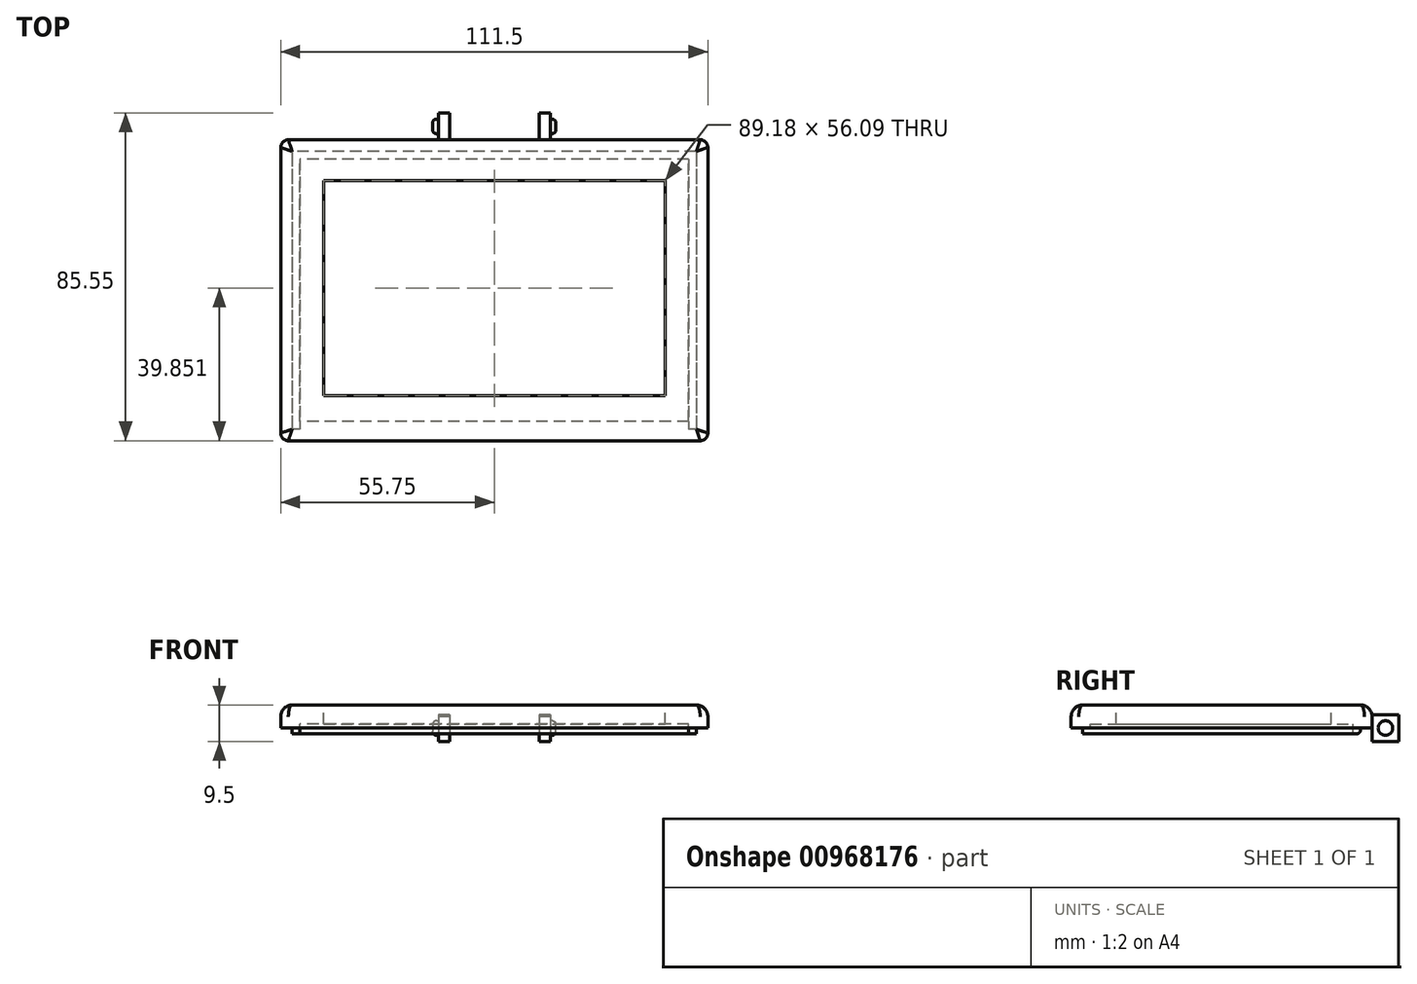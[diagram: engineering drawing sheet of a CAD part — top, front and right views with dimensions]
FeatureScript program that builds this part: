
annotation { "Feature Type Name" : "Feature", "Feature Type Description" : "" }
export const myFeature = defineFeature(function(context is Context, id is Id, definition is map)
    precondition{}
    {
        {
            var Q0;
            Q0=qCreatedBy(makeId("Top.planeOp"),FACE);
            cPlane(context, id + "F0", {"entities" : qUnion([Q0]), "cplaneType" : CPlaneType.OFFSET, "offset" : 3.5 * mm, "width" : 150 * mm, "height" : 150 * mm});
        }
        {
            var Q0;
            Q0=qCreatedBy(id+"F0.planeOp",FACE);
            var sketch = newSketch(context, id + "F1", { "sketchPlane" : qUnion([Q0])});
            skLineSegment(sketch, "E0.bottom", {"start": v(47.75, 31.27) * mm, "end": v(-47.75, 31.27) * mm});
            skLineSegment(sketch, "E0.top", {"start": v(47.75, -31.27) * mm, "end": v(-47.75, -31.27) * mm});
            skLineSegment(sketch, "E0.left", {"start": v(47.75, 31.27) * mm, "end": v(47.75, -31.27) * mm});
            skLineSegment(sketch, "E0.right", {"start": v(-47.75, 31.27) * mm, "end": v(-47.75, -31.27) * mm});
            skPoint(sketch, "E0.middle", {"position": v(0, 0) * mm});
            skLineSegment(sketch, "E1.0", {"start": v(-55.75, 39.27) * mm, "end": v(-55.75, -39.27) * mm});
            skLineSegment(sketch, "E1.1", {"start": v(55.75, 39.27) * mm, "end": v(-55.75, 39.27) * mm});
            skLineSegment(sketch, "E1.2", {"start": v(55.75, 39.27) * mm, "end": v(55.75, -39.27) * mm});
            skLineSegment(sketch, "E1.3", {"start": v(55.75, -39.27) * mm, "end": v(-55.75, -39.27) * mm});
            skSolve(sketch);
        }
        {
            var Q0;
            Q0=qCreatedBy(id+"F0.planeOp",FACE);
            var sketch = newSketch(context, id + "F2", { "sketchPlane" : qUnion([Q0])});
            skLineSegment(sketch, "E2.0", {"start": v(55.75, 39.27) * mm, "end": v(-55.75, 39.27) * mm});
            skLineSegment(sketch, "E3.0", {"start": v(-55.75, 39.27) * mm, "end": v(-55.75, -39.27) * mm});
            skLineSegment(sketch, "E4.0", {"start": v(55.75, -39.27) * mm, "end": v(-55.75, -39.27) * mm});
            skLineSegment(sketch, "E5.0", {"start": v(55.75, 39.27) * mm, "end": v(55.75, -39.27) * mm});
            skSolve(sketch);
        }
        {
            var Q0;
            Q0 = qSketchRegion(id + "F2", true);
            extrude(context, id + "F3", {"entities" : qUnion([Q0]), "depth" : 6 * mm, "offsetDistance" : 25 * mm});
        }
        {
            var Q0;
            Q0=makeQuery(id+"F3.opExtrude","CAP_FACE",FACE,{"disambiguationData":[OSD([sQuery(id+"F2.wireOp",EDGE,"E2.0"),sQuery(id+"F2.wireOp",EDGE,"E3.0"),sQuery(id+"F2.wireOp",EDGE,"E4.0"),sQuery(id+"F2.wireOp",EDGE,"E5.0")])],"isStart":false});
            fillet(context, id + "F4", {"entities" : qUnion([Q0]), "radius" : 3 * mm, "tangentPropagation" : true, "allowEdgeOverflow" : false});
        }
        {
            var Q0;
            Q0=makeQuery(id+"F4.opFillet","BLEND_EDGE",EDGE,{"blendedFrom":[makeQuery(id+"F3.opExtrude","CAP_EDGE",EDGE,{"disambiguationData":[OSD([sQuery(id+"F2.wireOp",EDGE,"E4.0")])],"isStart":false}),makeQuery(id+"F3.opExtrude","CAP_EDGE",EDGE,{"disambiguationData":[OSD([sQuery(id+"F2.wireOp",EDGE,"E5.0")])],"isStart":false})],"blendedInto":[]});
            var Q1;
            Q1=makeQuery(id+"F4.opFillet","BLEND_EDGE",EDGE,{"blendedFrom":[makeQuery(id+"F3.opExtrude","CAP_EDGE",EDGE,{"disambiguationData":[OSD([sQuery(id+"F2.wireOp",EDGE,"E2.0")])],"isStart":false}),makeQuery(id+"F3.opExtrude","CAP_EDGE",EDGE,{"disambiguationData":[OSD([sQuery(id+"F2.wireOp",EDGE,"E5.0")])],"isStart":false})],"blendedInto":[]});
            var Q2;
            Q2=makeQuery(id+"F4.opFillet","BLEND_EDGE",EDGE,{"blendedFrom":[makeQuery(id+"F3.opExtrude","CAP_EDGE",EDGE,{"disambiguationData":[OSD([sQuery(id+"F2.wireOp",EDGE,"E3.0")])],"isStart":false}),makeQuery(id+"F3.opExtrude","CAP_EDGE",EDGE,{"disambiguationData":[OSD([sQuery(id+"F2.wireOp",EDGE,"E4.0")])],"isStart":false})],"blendedInto":[]});
            var Q3;
            Q3=makeQuery(id+"F4.opFillet","BLEND_EDGE",EDGE,{"blendedFrom":[makeQuery(id+"F3.opExtrude","CAP_EDGE",EDGE,{"disambiguationData":[OSD([sQuery(id+"F2.wireOp",EDGE,"E2.0")])],"isStart":false}),makeQuery(id+"F3.opExtrude","CAP_EDGE",EDGE,{"disambiguationData":[OSD([sQuery(id+"F2.wireOp",EDGE,"E3.0")])],"isStart":false})],"blendedInto":[]});
            fillet(context, id + "F5", {"entities" : qUnion([Q0, Q1, Q2, Q3]), "radius" : 2 * mm, "tangentPropagation" : true, "allowEdgeOverflow" : false});
        }
        {
            var Q0;
            Q0=makeQuery(id+"F3.opExtrude","CAP_FACE",FACE,{"disambiguationData":[OSD([sQuery(id+"F2.wireOp",EDGE,"E2.0"),sQuery(id+"F2.wireOp",EDGE,"E3.0"),sQuery(id+"F2.wireOp",EDGE,"E4.0"),sQuery(id+"F2.wireOp",EDGE,"E5.0")])],"isStart":true});
            shell(context, id + "F6", {"entities" : qUnion([Q0]), "thickness" : 5 * mm});
        }
        {
            var Q0;
            Q0=qCreatedBy(id+"F0.planeOp",FACE);
            var sketch = newSketch(context, id + "F7", { "sketchPlane" : qUnion([Q0])});
            skLineSegment(sketch, "E6.0", {"start": v(50.75, -34.27) * mm, "end": v(-50.75, -34.27) * mm});
            skLineSegment(sketch, "E7.0", {"start": v(50.75, 34.27) * mm, "end": v(50.75, -34.27) * mm});
            skLineSegment(sketch, "E8.0", {"start": v(50.75, 34.27) * mm, "end": v(-50.75, 34.27) * mm});
            skLineSegment(sketch, "E9.0", {"start": v(-50.75, 34.27) * mm, "end": v(-50.75, -34.27) * mm});
            skLineSegment(sketch, "E10.0", {"start": v(52.75, -36.27) * mm, "end": v(-52.75, -36.27) * mm});
            skLineSegment(sketch, "E10.1", {"start": v(52.75, 36.27) * mm, "end": v(52.75, -36.27) * mm});
            skLineSegment(sketch, "E10.2", {"start": v(52.75, 36.27) * mm, "end": v(-52.75, 36.27) * mm});
            skLineSegment(sketch, "E10.3", {"start": v(-52.75, 36.27) * mm, "end": v(-52.75, -36.27) * mm});
            skLineSegment(sketch, "E11.0", {"start": v(-50.75, -34.27) * mm, "end": v(50.75, -34.27) * mm});
            skLineSegment(sketch, "E11.3", {"start": v(50.75, -34.27) * mm, "end": v(50.75, 34.27) * mm});
            skSolve(sketch);
        }
        {
            var Q0;
            Q0 = qSketchRegion(id + "F7", true);
            extrude(context, id + "F8", {"entities" : qUnion([Q0]), "operationType" : NewBodyOperationType.ADD, "oppositeDirection" : true, "depth" : 1.5 * mm, "offsetDistance" : 25 * mm});
        }
        {
            var Q0;
            Q0=makeQuery(id+"F8.opExtrude","CAP_EDGE",EDGE,{"disambiguationData":[OSD([sQuery(id+"F7.wireOp",EDGE,"E10.2")])],"isStart":false});
            fillet(context, id + "F9", {"entities" : qUnion([Q0]), "radius" : 1 * mm, "tangentPropagation" : true, "allowEdgeOverflow" : false});
        }
        {
            var Q0;
            Q0=makeQuery(id+"F8.opExtrude","CAP_FACE",FACE,{"disambiguationData":[OSD([sQuery(id+"F7.wireOp",EDGE,"E10.0"),sQuery(id+"F7.wireOp",EDGE,"E10.1"),sQuery(id+"F7.wireOp",EDGE,"E10.2"),sQuery(id+"F7.wireOp",EDGE,"E10.3"),sQuery(id+"F7.wireOp",EDGE,"E11.0"),sQuery(id+"F7.wireOp",EDGE,"E9.0"),sQuery(id+"F7.wireOp",EDGE,"E8.0"),sQuery(id+"F7.wireOp",EDGE,"E11.3")])],"isStart":false});
            var sketch = newSketch(context, id + "F10", { "sketchPlane" : qUnion([Q0])});
            skLineSegment(sketch, "E12.0", {"start": v(-50.75, 34.27) * mm, "end": v(50.75, 34.27) * mm});
            skLineSegment(sketch, "E13.0", {"start": v(50.75, 36.27) * mm, "end": v(-50.75, 36.27) * mm});
            skLineSegment(sketch, "E14", {"start": v(-50.75, 34.27) * mm, "end": v(-50.75, 36.27) * mm});
            skLineSegment(sketch, "E15", {"start": v(50.75, 34.27) * mm, "end": v(50.75, 36.27) * mm});
            skPoint(sketch, "E16.orphan", {"position": v(52.75, 36.27) * mm});
            skPoint(sketch, "E17.orphan", {"position": v(-52.75, 36.27) * mm});
            skSolve(sketch);
        }
        {
            var Q0;
            Q0 = qSketchRegion(id + "F10", true);
            extrude(context, id + "F11", {"entities" : qUnion([Q0]), "operationType" : NewBodyOperationType.REMOVE, "oppositeDirection" : true, "depth" : 1.5 * mm, "offsetDistance" : 25 * mm});
        }
        {
            var Q0;
            Q0=makeQuery(id+"F3.opExtrude","CAP_FACE",FACE,{"disambiguationData":[OSD([sQuery(id+"F2.wireOp",EDGE,"E2.0"),sQuery(id+"F2.wireOp",EDGE,"E3.0"),sQuery(id+"F2.wireOp",EDGE,"E4.0"),sQuery(id+"F2.wireOp",EDGE,"E5.0")])],"isStart":false});
            var sketch = newSketch(context, id + "F12", { "sketchPlane" : qUnion([Q0])});
            skLineSegment(sketch, "E18.bottom", {"start": v(44.6, 28.61) * mm, "end": v(-44.6, 28.61) * mm});
            skLineSegment(sketch, "E18.top", {"start": v(44.6, -27.47) * mm, "end": v(-44.6, -27.47) * mm});
            skLineSegment(sketch, "E18.left", {"start": v(44.6, 28.61) * mm, "end": v(44.6, -27.47) * mm});
            skLineSegment(sketch, "E18.right", {"start": v(-44.6, 28.61) * mm, "end": v(-44.6, -27.47) * mm});
            skPoint(sketch, "E18.middle", {"position": v(0, 0.57) * mm});
            skPoint(sketch, "E18.middle.positionSnap0", {"position": v(0, 36.27) * mm});
            skPoint(sketch, "E18.centerSnap0", {"position": v(0, 36.27) * mm});
            skSolve(sketch);
        }
        {
            var Q0;
            Q0 = qSketchRegion(id + "F12", true);
            extrude(context, id + "F13", {"entities" : qUnion([Q0]), "operationType" : NewBodyOperationType.REMOVE, "endBound" : BoundingType.UP_TO_NEXT, "oppositeDirection" : true, "depth" : 25 * mm, "offsetDistance" : 25 * mm});
        }
        {
            var Q0;
            Q0=makeQuery(id+"F1.imprint","IMPRINT",FACE,{"disambiguationData":[TD([[makeQuery(id+"F1.imprint","IMPRINT",EDGE,{"derivedFrom":sQuery(id+"F1.wireOp",EDGE,"E0.bottom")}),-1.0]])]});
            var sketch = newSketch(context, id + "F14", { "sketchPlane" : qUnion([Q0])});
            skLineSegment(sketch, "E19.0", {"start": v(55.75, 39.27) * mm, "end": v(-55.75, 39.27) * mm, "construction": true});
            skLineSegment(sketch, "E20.bottom", {"start": v(14.6, 39.27) * mm, "end": v(11.7, 39.27) * mm});
            skLineSegment(sketch, "E20.top", {"start": v(14.6, 46.27) * mm, "end": v(11.7, 46.27) * mm});
            skLineSegment(sketch, "E20.left", {"start": v(14.6, 39.27) * mm, "end": v(14.6, 46.27) * mm});
            skLineSegment(sketch, "E20.right", {"start": v(11.7, 39.27) * mm, "end": v(11.7, 46.27) * mm});
            skLineSegment(sketch, "E21.MirrorCS", {"start": v(-11.7, 39.27) * mm, "end": v(-11.7, 46.27) * mm});
            skLineSegment(sketch, "E22.MirrorCS", {"start": v(-14.6, 39.27) * mm, "end": v(-11.7, 39.27) * mm});
            skLineSegment(sketch, "E23.MirrorCS", {"start": v(-14.6, 46.27) * mm, "end": v(-11.7, 46.27) * mm});
            skLineSegment(sketch, "E24.MirrorCS", {"start": v(-14.6, 39.27) * mm, "end": v(-14.6, 46.27) * mm});
            skSolve(sketch);
        }
        {
            var Q0;
            Q0 = qSketchRegion(id + "F14", true);
            extrude(context, id + "F15", {"entities" : qUnion([Q0]), "operationType" : NewBodyOperationType.ADD, "endBound" : BoundingType.SYMMETRIC, "depth" : 7 * mm, "offsetDistance" : 25 * mm});
        }
        {
            var Q0;
            Q0=makeQuery(id+"F15.opExtrude","SWEPT_FACE",FACE,{"disambiguationData":[OSD([sQuery(id+"F14.wireOp",EDGE,"E24.MirrorCS")])]});
            var sketch = newSketch(context, id + "F16", { "sketchPlane" : qUnion([Q0])});
            skPoint(sketch, "E25", {"position": v(-42.77, 7) * mm});
            skPoint(sketch, "E26", {"position": v(-46.27, 3.5) * mm});
            skCircle(sketch, "E27", {"center": v(-42.77, 3.5) * mm, "radius": 1.9 * mm});
            skSolve(sketch);
        }
        {
            var Q0;
            Q0 = qSketchRegion(id + "F16", true);
            extrude(context, id + "F17", {"entities" : qUnion([Q0]), "operationType" : NewBodyOperationType.ADD, "depth" : 1.5 * mm, "offsetDistance" : 25 * mm});
        }
        {
            var Q0;
            Q0=makeQuery(id+"F17.opExtrude","CAP_EDGE",EDGE,{"disambiguationData":[OSD([sQuery(id+"F16.wireOp",EDGE,"E27")])],"isStart":false});
            fillet(context, id + "F18", {"entities" : qUnion([Q0]), "radius" : 1 * mm, "tangentPropagation" : true, "allowEdgeOverflow" : false});
        }
        {
            var Q0;
            Q0=makeQuery(id+"F15.opExtrude","SWEPT_FACE",FACE,{"disambiguationData":[OSD([sQuery(id+"F14.wireOp",EDGE,"E20.left")])]});
            var sketch = newSketch(context, id + "F19", { "sketchPlane" : qUnion([Q0])});
            skPoint(sketch, "E28", {"position": v(42.77, 7) * mm});
            skPoint(sketch, "E29", {"position": v(46.27, 3.5) * mm});
            skCircle(sketch, "E30", {"center": v(42.77, 3.5) * mm, "radius": 1.9 * mm});
            skSolve(sketch);
        }
        {
            var Q0;
            Q0 = qSketchRegion(id + "F19", true);
            extrude(context, id + "F20", {"entities" : qUnion([Q0]), "operationType" : NewBodyOperationType.ADD, "depth" : 1.5 * mm, "offsetDistance" : 25 * mm});
        }
        {
            var Q0;
            Q0=makeQuery(id+"F20.opExtrude","CAP_EDGE",EDGE,{"disambiguationData":[OSD([sQuery(id+"F19.wireOp",EDGE,"E30")])],"isStart":false});
            fillet(context, id + "F21", {"entities" : qUnion([Q0]), "radius" : 1 * mm, "tangentPropagation" : true, "allowEdgeOverflow" : false});
        }
    });
